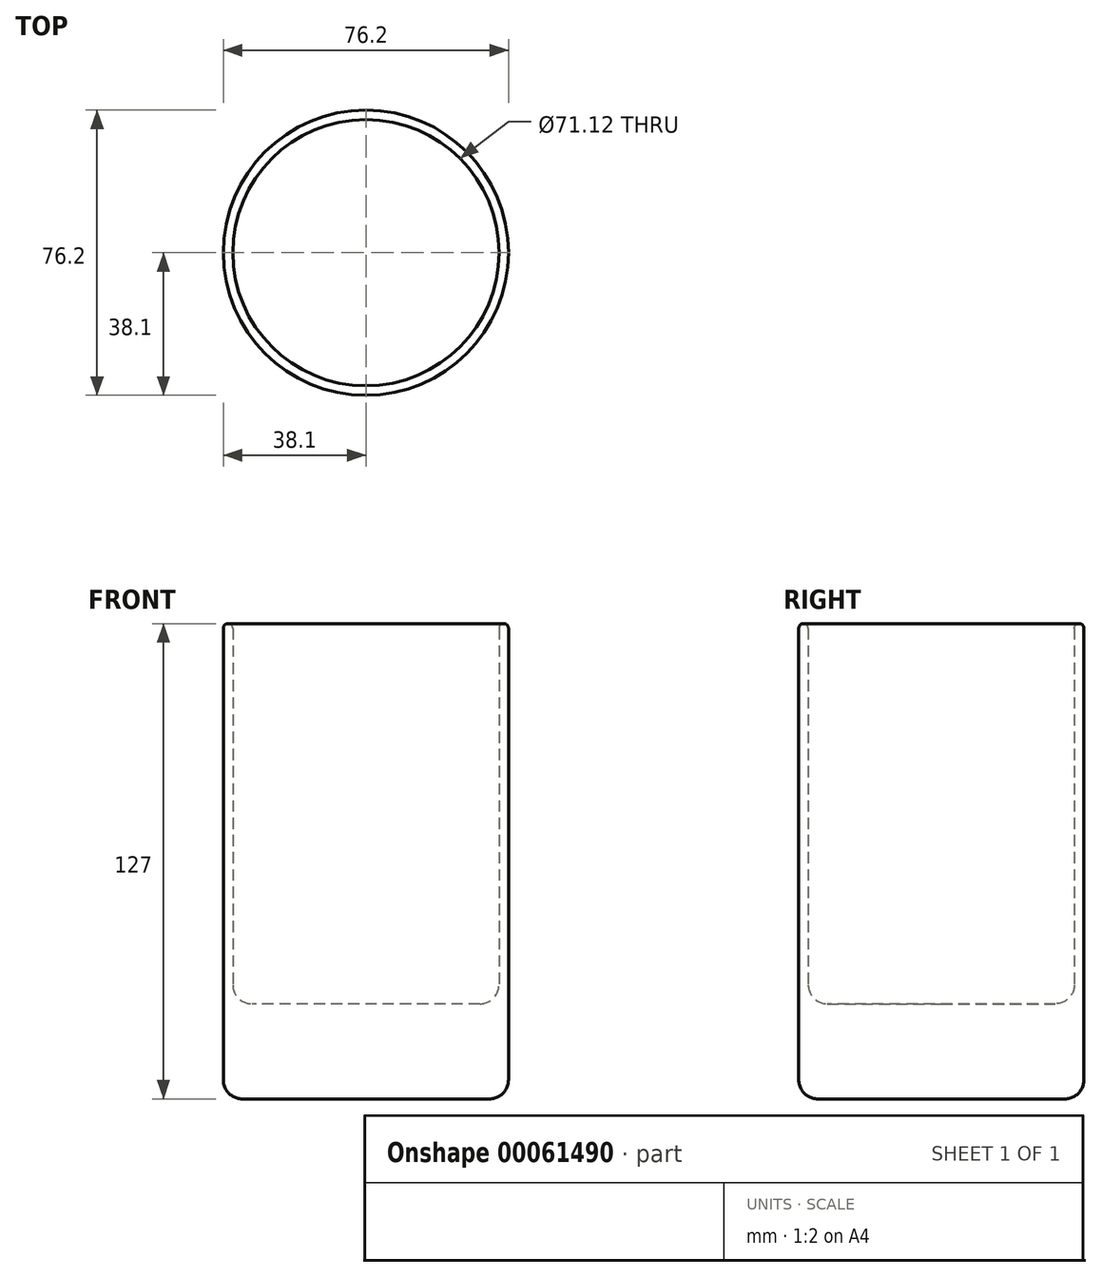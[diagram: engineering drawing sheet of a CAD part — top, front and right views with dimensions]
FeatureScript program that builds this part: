
annotation { "Feature Type Name" : "Feature", "Feature Type Description" : "" }
export const myFeature = defineFeature(function(context is Context, id is Id, definition is map)
    precondition{}
    {
        {
            var Q0;
            Q0=qCreatedBy(makeId("Top.planeOp"),FACE);
            var sketch = newSketch(context, id + "F0", { "sketchPlane" : qUnion([Q0])});
            skCircle(sketch, "E0", {"center": v(0, 0) * mm, "radius": 38.1 * mm});
            skCircle(sketch, "E1", {"center": v(0, 0) * mm, "radius": 35.56 * mm});
            skSolve(sketch);
        }
        {
            var Q0;
            Q0=makeQuery(id+"F0.imprint","IMPRINT",FACE,{"disambiguationData":[TD([[makeQuery(id+"F0.imprint","IMPRINT",EDGE,{"derivedFrom":sQuery(id+"F0.wireOp",EDGE,"E0")}),1.0]])]});
            extrude(context, id + "F1", {"entities" : qUnion([Q0]), "depth" : 127 * mm});
        }
        {
            var Q0;
            Q0=qCreatedBy(makeId("Top.planeOp"),FACE);
            var sketch = newSketch(context, id + "F2", { "sketchPlane" : qUnion([Q0])});
            skCircle(sketch, "E2", {"center": v(0, 0) * mm, "radius": 38.1 * mm});
            skSolve(sketch);
        }
        {
            var Q0;
            Q0=makeQuery(id+"F2.imprint","IMPRINT",FACE,{"disambiguationData":[TD([[makeQuery(id+"F2.imprint","IMPRINT",EDGE,{"derivedFrom":sQuery(id+"F2.wireOp",EDGE,"E2")}),1.0]])]});
            extrude(context, id + "F3", {"entities" : qUnion([Q0]), "operationType" : NewBodyOperationType.ADD, "depth" : 25.4 * mm});
        }
        {
            var Q0;
            Q0=makeQuery(id+"F1.opExtrude","CAP_EDGE",EDGE,{"disambiguationData":[OSD([sQuery(id+"F0.wireOp",EDGE,"E0")])],"isStart":false});
            var Q1;
            Q1=makeQuery(id+"F1.opExtrude","CAP_EDGE",EDGE,{"disambiguationData":[OSD([sQuery(id+"F0.wireOp",EDGE,"E1")])],"isStart":false});
            fillet(context, id + "F4", {"entities" : qUnion([Q0, Q1]), "radius" : 1.27 * mm, "tangentPropagation" : true, "allowEdgeOverflow" : false});
        }
        {
            var Q0;
            Q0=makeQuery(id+"F1.opExtrude","CAP_EDGE",EDGE,{"disambiguationData":[OSD([sQuery(id+"F0.wireOp",EDGE,"E0")])],"isStart":true});
            fillet(context, id + "F5", {"entities" : qUnion([Q0]), "radius" : 5.08 * mm, "tangentPropagation" : true, "allowEdgeOverflow" : false});
        }
        {
            var Q0;
            Q0=makeQuery(id+"F3.boolean.opBoolean","INTERSECT",EDGE,{"derivedFrom":[makeQuery(id+"F1.opExtrude","SWEPT_FACE",FACE,{"disambiguationData":[OSD([sQuery(id+"F0.wireOp",EDGE,"E1")])]}),makeQuery(id+"F3.opExtrude","CAP_FACE",FACE,{"disambiguationData":[OSD([sQuery(id+"F2.wireOp",EDGE,"E2")])],"isStart":false})]});
            fillet(context, id + "F6", {"entities" : qUnion([Q0]), "radius" : 5.08 * mm, "tangentPropagation" : true, "allowEdgeOverflow" : false});
        }
    });
